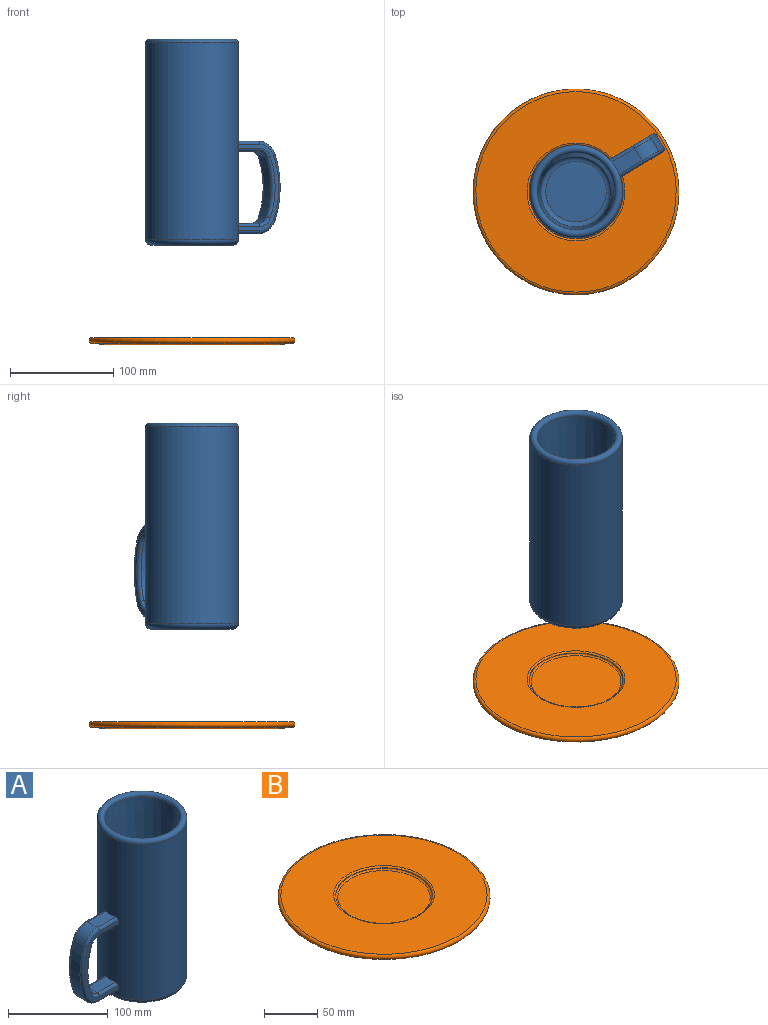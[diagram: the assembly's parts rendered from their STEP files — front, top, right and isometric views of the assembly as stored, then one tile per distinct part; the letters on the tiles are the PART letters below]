
ASSEMBLY  parts=2 mates=1
PART A: 39 faces, bbox 151.1x97.4x200 mm
  f0: cylinder r=45mm len=191.25mm, axis (0,0,1), area 53686.8mm2, adj f1,f6,f7,f8,f9,f10,f11,f12
  f1: torus R=40mm, axis (0,0,1), area 2131mm2, adj f0,f2
  f2: plane 80x80mm, normal (0,0,-1), area 5026.5mm2, adj f1
  f3: plane 58.61x58.61mm, normal (0,0,1), area 2698.1mm2, adj f4
  f4: torus R=29.31mm, axis (0,0,1), area 1565.6mm2, adj f3,f5
  f5: cone r=37.5mm half-angle=2deg, axis (0,0,1), area 20665mm2, adj f4,f6
  f6: torus R=41.25mm, axis (0,0,1), area 3023.4mm2, adj f0,f5
  f7: cylinder r=3mm len=26.51mm, axis (-1,0,0), area 123.9mm2, adj f0,f8,f18,f19
  f8: plane 84x48.13mm, normal (0,1,0), area 605.1mm2, adj f0,f7,f9,f13,f14,f19,f20,f25
  f9: cylinder r=3mm len=26.51mm, axis (-1,0,0), area 123.9mm2, adj f0,f8,f17,f20
  f10: cylinder r=3mm len=26.51mm, axis (-1,0,0), area 123.9mm2, adj f0,f11,f17,f22
  f11: plane 84x48.13mm, normal (0,-1,0), area 605.1mm2, adj f0,f10,f12,f15,f16,f22,f23,f28
  f12: cylinder r=3mm len=26.51mm, axis (-1,0,0), area 123.9mm2, adj f0,f11,f18,f23
  f13: cylinder r=3mm len=26.51mm, axis (1,0,0), area 123.9mm2, adj f0,f8,f31,f38
  f14: cylinder r=3mm len=26.51mm, axis (1,0,0), area 123.9mm2, adj f0,f8,f32,f37
  f15: cylinder r=3mm len=26.51mm, axis (1,0,0), area 123.9mm2, adj f0,f11,f34,f37
  f16: cylinder r=3mm len=26.51mm, axis (1,0,0), area 123.9mm2, adj f0,f11,f35,f38
  f17: plane 25.93x14mm, normal (0,0,-1), area 357.9mm2, adj f0,f9,f10,f21
  f18: plane 25.93x14mm, normal (0,0,1), area 357.9mm2, adj f0,f7,f12,f24
  f19: torus R=17mm, axis (0,-1,0), area 107.4mm2, adj f7,f8,f24,f25
  f20: torus R=13mm, axis (0,-1,0), area 63mm2, adj f8,f9,f21,f26
  f21: cylinder r=10mm len=14mm, axis (0,-1,0), area 168.8mm2, adj f17,f20,f22,f27
  f22: torus R=13mm, axis (0,-1,0), area 63mm2, adj f10,f11,f21,f28
  f23: torus R=17mm, axis (0,-1,0), area 107.4mm2, adj f11,f12,f24,f29
  f24: cylinder r=20mm len=18.68mm, axis (0,-1,0), area 337.6mm2, adj f18,f19,f23,f30
  f25: torus R=87mm, axis (0,-1,0), area 306mm2, adj f8,f19,f30,f31
  f26: torus R=83mm, axis (0,-1,0), area 279.1mm2, adj f8,f20,f27,f32
  f27: cylinder r=80mm len=57.14mm, axis (0,-1,0), area 818.1mm2, adj f21,f26,f28,f33
  f28: torus R=83mm, axis (0,-1,0), area 279.1mm2, adj f11,f22,f27,f34
  f29: torus R=87mm, axis (0,-1,0), area 306mm2, adj f11,f23,f30,f35
  f30: cylinder r=90mm len=64.29mm, axis (0,-1,0), area 920.3mm2, adj f24,f25,f29,f36
  f31: torus R=17mm, axis (0,-1,0), area 107.4mm2, adj f8,f13,f25,f36
  f32: torus R=13mm, axis (0,-1,0), area 63mm2, adj f8,f14,f26,f33
  f33: cylinder r=10mm len=14mm, axis (0,-1,0), area 168.8mm2, adj f27,f32,f34,f37
  f34: torus R=13mm, axis (0,-1,0), area 63mm2, adj f11,f15,f28,f33
  f35: torus R=17mm, axis (0,-1,0), area 107.4mm2, adj f11,f16,f29,f36
  f36: cylinder r=20mm len=18.68mm, axis (0,-1,0), area 337.6mm2, adj f30,f31,f35,f38
  f37: plane 25.93x14mm, normal (0,0,1), area 357.9mm2, adj f0,f14,f15,f33
  f38: plane 25.93x14mm, normal (0,0,-1), area 357.9mm2, adj f0,f13,f16,f36
PART B: 8 faces, bbox 216.5x216.5x7 mm
  f0: plane 160x160mm, normal (0,0,-1), area 20106.2mm2, adj f1
  f1: cone r=80mm half-angle=85deg, axis (0,0,1), area 9795.3mm2, adj f0,f2
  f2: torus R=97.26mm, axis (0,0,-1), area 5207.9mm2, adj f1,f3
  f3: plane 194.52x194.52mm, normal (0,0,1), area 22629.9mm2, adj f2,f4
  f4: torus R=47.5mm, axis (0,0,-1), area 712.7mm2, adj f3,f5
  f5: cone r=45.49mm half-angle=20deg, axis (0,0,1), area 112.1mm2, adj f4,f6
  f6: torus R=43.61mm, axis (0,0,-1), area 686mm2, adj f5,f7
  f7: plane 87.21x87.21mm, normal (0,0,1), area 5974mm2, adj f6
PLACE A rot(axis=(0,0,-1),149.3deg) t=(0,0,92.97)mm
PLACE B rot(axis=(0,0,1),90deg) t=(0,0,-4)mm
MATE cylindrical B.f1 <-> A.f0  axis (0,0,1) through (0,0,0)mm
